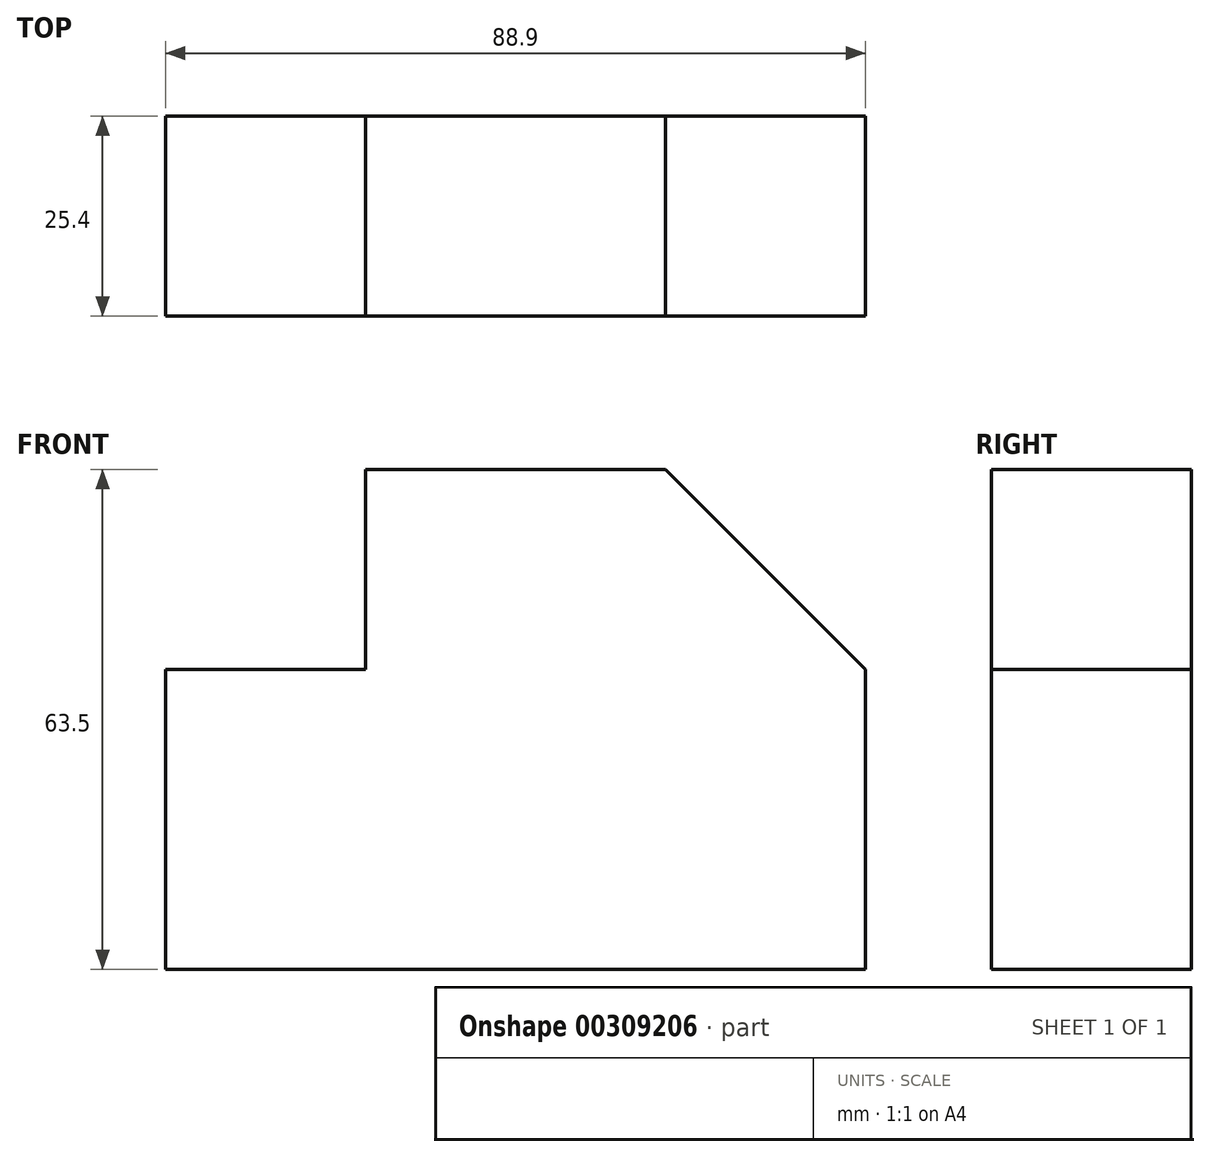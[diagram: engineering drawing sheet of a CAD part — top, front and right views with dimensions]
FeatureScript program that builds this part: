
annotation { "Feature Type Name" : "Feature", "Feature Type Description" : "" }
export const myFeature = defineFeature(function(context is Context, id is Id, definition is map)
    precondition{}
    {
        {
            var Q0;
            Q0=qCreatedBy(makeId("Front.planeOp"),FACE);
            var sketch = newSketch(context, id + "F0", { "sketchPlane" : qUnion([Q0])});
            skLineSegment(sketch, "E0", {"start": v(19.96, 19.38) * mm, "end": v(-18.14, 19.38) * mm});
            skLineSegment(sketch, "E1", {"start": v(-18.14, 19.38) * mm, "end": v(-18.14, -6.02) * mm});
            skLineSegment(sketch, "E2", {"start": v(-18.14, -6.02) * mm, "end": v(-43.54, -6.02) * mm});
            skLineSegment(sketch, "E3", {"start": v(-43.54, -44.12) * mm, "end": v(-43.54, -6.02) * mm});
            skLineSegment(sketch, "E4", {"start": v(-43.54, -44.12) * mm, "end": v(45.36, -44.12) * mm});
            skLineSegment(sketch, "E5", {"start": v(45.36, -44.12) * mm, "end": v(45.36, -6.02) * mm});
            skLineSegment(sketch, "E6", {"start": v(45.36, -6.02) * mm, "end": v(19.96, 19.38) * mm});
            skSolve(sketch);
        }
        {
            var Q0;
            Q0=makeQuery(id+"F0.imprint","IMPRINT",FACE,{"disambiguationData":[TD([[makeQuery(id+"F0.imprint","IMPRINT",EDGE,{"derivedFrom":sQuery(id+"F0.wireOp",EDGE,"E0")}),1.0]])]});
            extrude(context, id + "F1", {"entities" : qUnion([Q0]), "depth" : 25.4 * mm});
        }
    });
